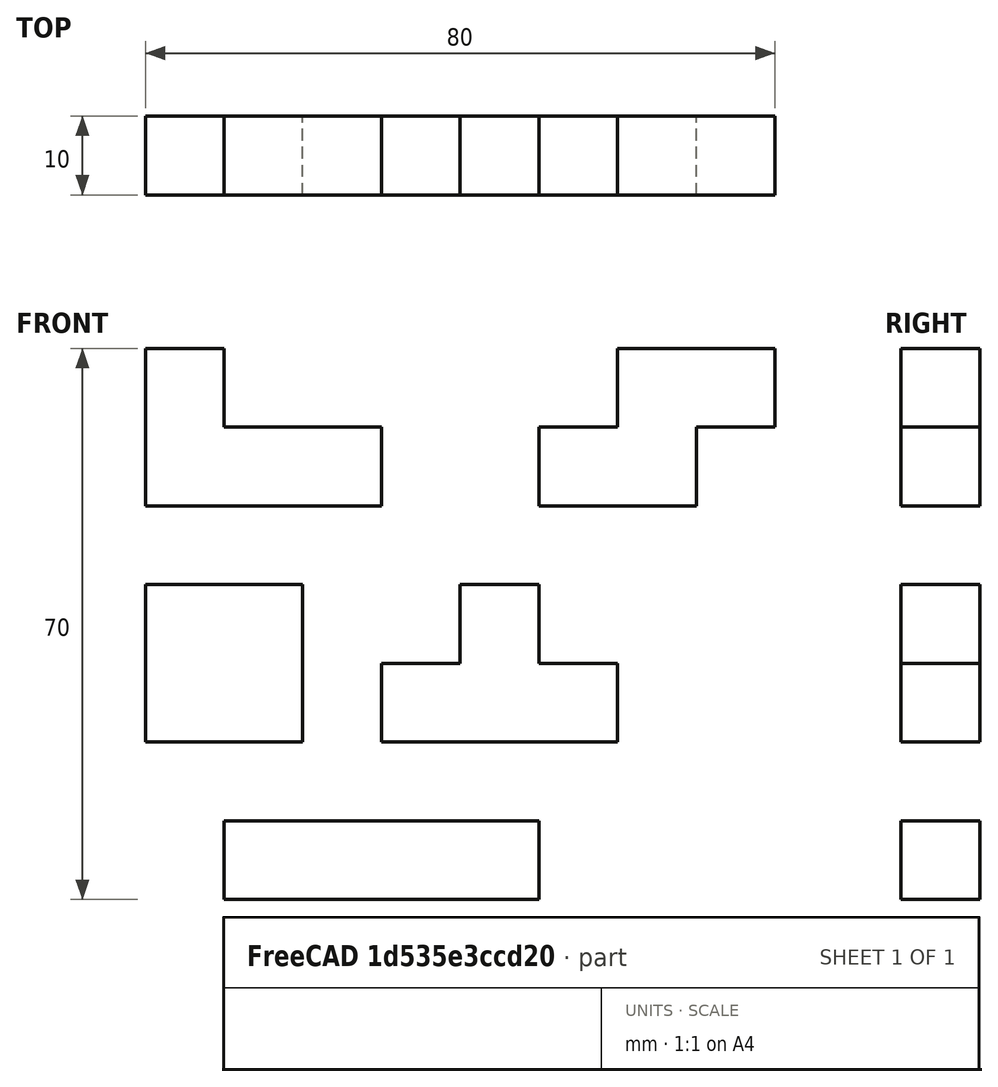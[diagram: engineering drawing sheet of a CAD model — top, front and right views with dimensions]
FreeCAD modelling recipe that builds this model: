
FCSTD DOCUMENT  (FreeCAD 0.21R33694 (Git))
Label: OJT1_T05R03
License: All rights reserved
LicenseURL: https://en.wikipedia.org/wiki/All_rights_reserved
objects: Part::Box×9, Part::MultiFuse×4, Part::Refine×4
note: 17 computed .brp shape members not serialized (recipe doc carries the construction recipe); baked Part::Feature solids carry a one-line shape summary decoded from their .brp

FEATURE [Part::Box] Box  label="Figura 1"
  AttacherType = Attacher::AttachEngine3D
  Height = 10
  Length = 40
  Width = 10
FEATURE [Part::Box] Box001  label="Cub"
  AttacherType = Attacher::AttachEngine3D
  Height = 10
  Length = 30
  Placement = pos=(20,0,20) rot=(0,0,1;0rad)
  Width = 10
FEATURE [Part::Box] Box002  label="Cub001"
  AttacherType = Attacher::AttachEngine3D
  Height = 10
  Length = 10
  Placement = pos=(30,0,30) rot=(0,0,1;0rad)
  Width = 10
FEATURE [Part::MultiFuse] Fusion  label="Figura 2"
  Shapes = -> [Box001,Box002]
FEATURE [Part::Refine] Fusion001  label="Figuraa 2"
  Source = -> Fusion
FEATURE [Part::Box] Box003  label="Cub002"
  AttacherType = Attacher::AttachEngine3D
  Height = 10
  Length = 20
  Placement = pos=(-10,0,20) rot=(0,0,1;0rad)
  Width = 10
FEATURE [Part::Box] Box004  label="Cub003"
  AttacherType = Attacher::AttachEngine3D
  Height = 10
  Length = 20
  Placement = pos=(-10,0,30) rot=(0,0,1;0rad)
  Width = 10
FEATURE [Part::MultiFuse] Fusion002  label="Figura 3"
  Shapes = -> [Box003,Box004]
FEATURE [Part::Refine] Fusion003  label="Figuraa 3"
  Source = -> Fusion002
FEATURE [Part::Box] Box005  label="Cub004"
  AttacherType = Attacher::AttachEngine3D
  Height = 10
  Length = 30
  Placement = pos=(-10,0,50) rot=(0,0,1;0rad)
  Width = 10
FEATURE [Part::Box] Box006  label="Cub005"
  AttacherType = Attacher::AttachEngine3D
  Height = 10
  Length = 10
  Placement = pos=(-10,0,60) rot=(0,0,1;0rad)
  Width = 10
FEATURE [Part::MultiFuse] Fusion004  label="Figura 4"
  Shapes = -> [Box005,Box006]
FEATURE [Part::Refine] Fusion005  label="Figuraa 4"
  Source = -> Fusion004
FEATURE [Part::Box] Box007  label="Cub006"
  AttacherType = Attacher::AttachEngine3D
  Height = 10
  Length = 20
  Placement = pos=(40,0,50) rot=(0,0,1;0rad)
  Width = 10
FEATURE [Part::Box] Box008  label="Cub007"
  AttacherType = Attacher::AttachEngine3D
  Height = 10
  Length = 20
  Placement = pos=(50,0,60) rot=(0,0,1;0rad)
  Width = 10
FEATURE [Part::MultiFuse] Fusion006  label="Figura 5"
  Shapes = -> [Box007,Box008]
FEATURE [Part::Refine] Fusion007  label="Figuraa 5"
  Source = -> Fusion006
